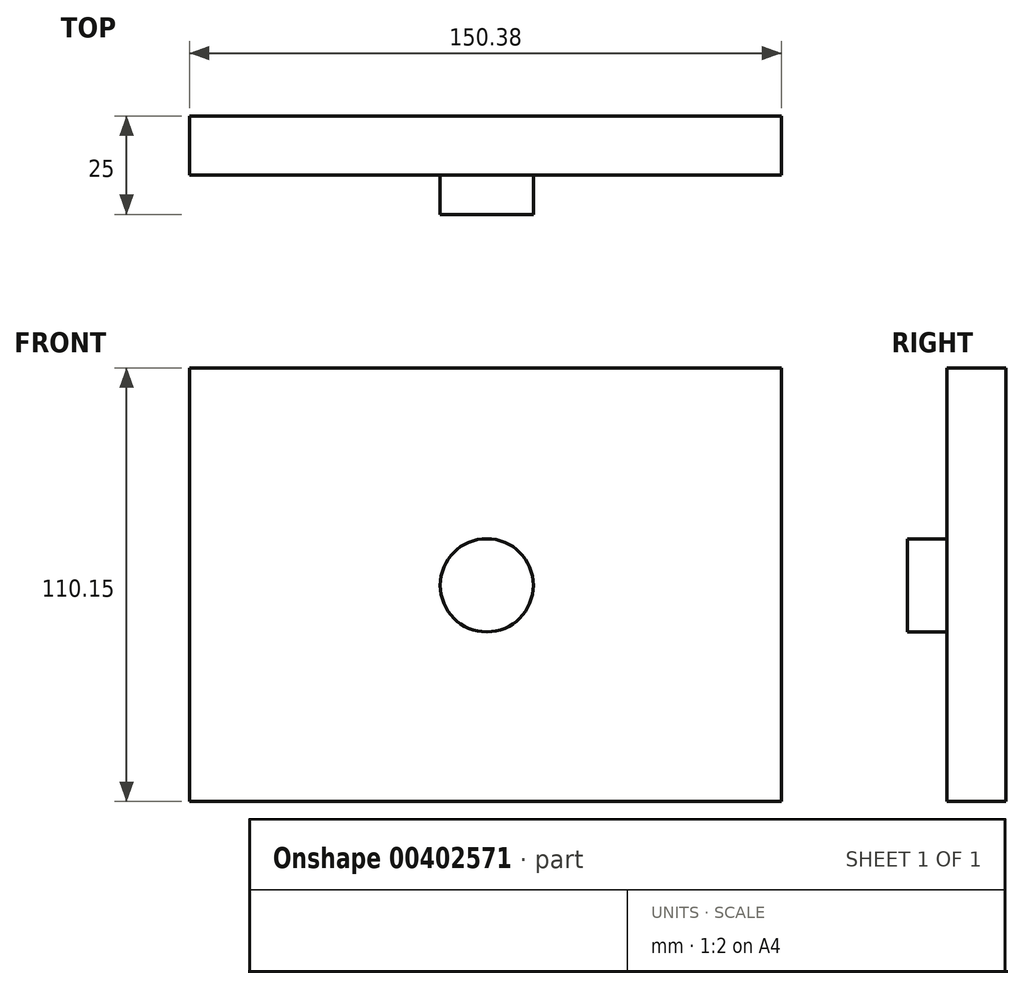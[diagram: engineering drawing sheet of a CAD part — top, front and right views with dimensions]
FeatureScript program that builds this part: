
annotation { "Feature Type Name" : "Feature", "Feature Type Description" : "" }
export const myFeature = defineFeature(function(context is Context, id is Id, definition is map)
    precondition{}
    {
        {
            var Q0;
            Q0=qCreatedBy(makeId("Front.planeOp"),FACE);
            var sketch = newSketch(context, id + "F0", { "sketchPlane" : qUnion([Q0])});
            skLineSegment(sketch, "E0.bottom", {"start": v(-75.5, 55.23) * mm, "end": v(74.88, 55.23) * mm});
            skLineSegment(sketch, "E0.top", {"start": v(-75.5, -54.92) * mm, "end": v(74.88, -54.92) * mm});
            skLineSegment(sketch, "E0.left", {"start": v(-75.5, 55.23) * mm, "end": v(-75.5, -54.92) * mm});
            skLineSegment(sketch, "E0.right", {"start": v(74.88, 55.23) * mm, "end": v(74.88, -54.92) * mm});
            skSolve(sketch);
        }
        {
            var Q0;
            Q0=makeQuery(id+"F0.imprint","IMPRINT",FACE,{"disambiguationData":[TD([[makeQuery(id+"F0.imprint","IMPRINT",EDGE,{"derivedFrom":sQuery(id+"F0.wireOp",EDGE,"E0.bottom")}),-1.0]])]});
            var sketch = newSketch(context, id + "F1", { "sketchPlane" : qUnion([Q0])});
            skCircle(sketch, "E1", {"center": v(0, 0) * mm, "radius": 11.83 * mm});
            skSolve(sketch);
        }
        {
            var Q0;
            Q0 = qSketchRegion(id + "F1", true);
            extrude(context, id + "F2", {"entities" : qUnion([Q0]), "depth" : 25 * mm});
        }
        {
            var Q0;
            Q0=makeQuery(id+"F0.imprint","IMPRINT",FACE,{"disambiguationData":[TD([[makeQuery(id+"F0.imprint","IMPRINT",EDGE,{"derivedFrom":sQuery(id+"F0.wireOp",EDGE,"E0.bottom")}),-1.0]])]});
            extrude(context, id + "F3", {"entities" : qUnion([Q0]), "operationType" : NewBodyOperationType.ADD, "depth" : 15 * mm});
        }
    });
